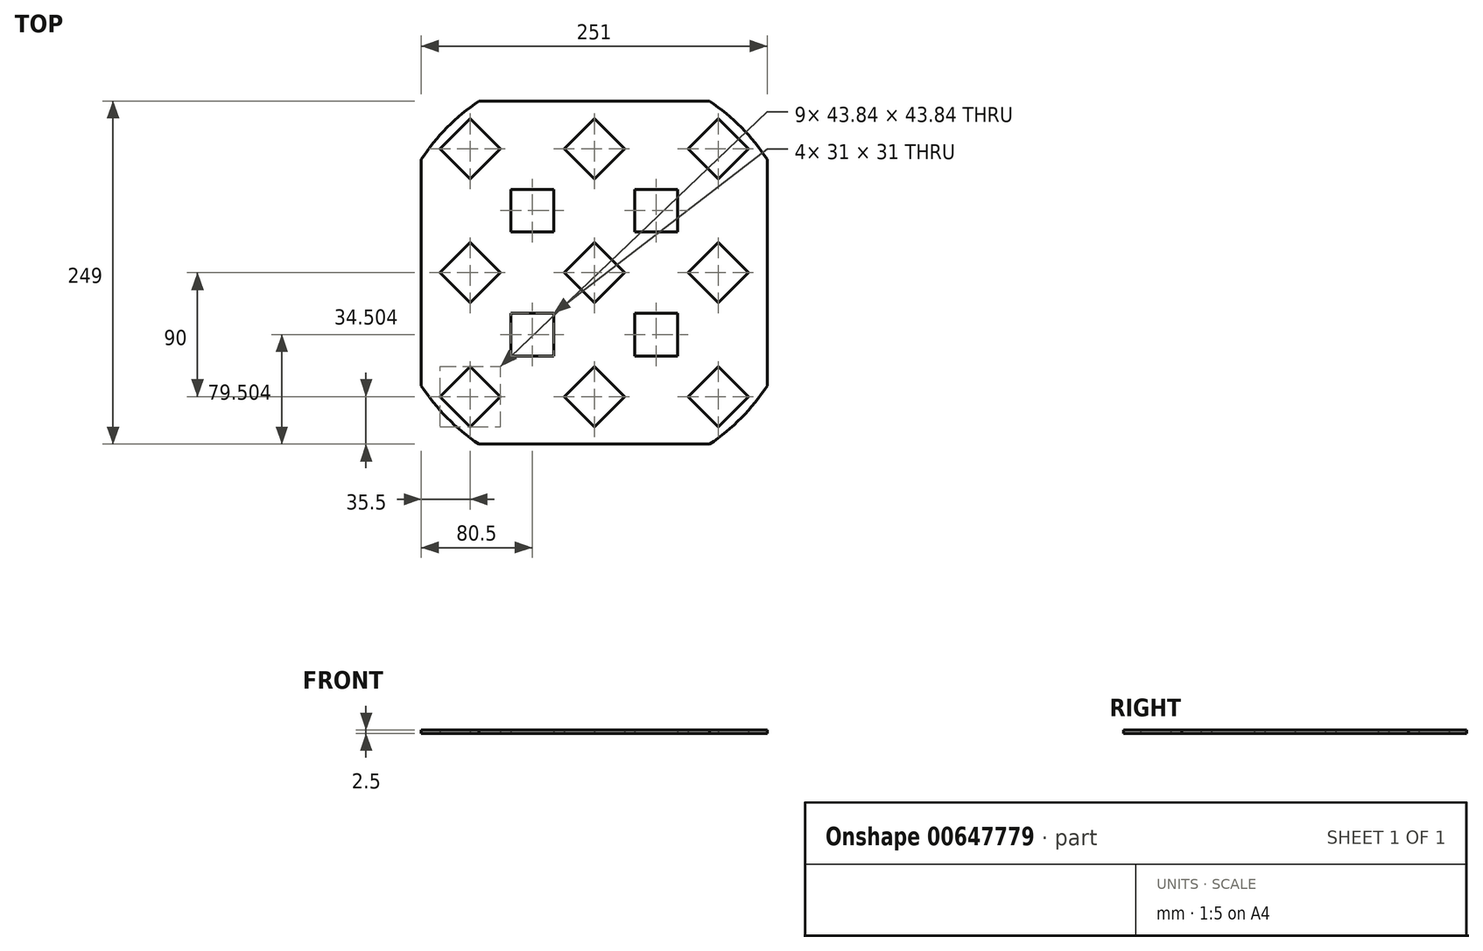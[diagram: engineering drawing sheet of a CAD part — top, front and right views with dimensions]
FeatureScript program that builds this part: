
annotation { "Feature Type Name" : "Feature", "Feature Type Description" : "" }
export const myFeature = defineFeature(function(context is Context, id is Id, definition is map)
    precondition{}
    {
        {
            var Q0;
            Q0=qCreatedBy(makeId("Top.planeOp"),FACE);
            var sketch = newSketch(context, id + "F0", { "sketchPlane" : qUnion([Q0])});
            skLineSegment(sketch, "E0.bottom", {"start": v(6.34, 193.08) * mm, "end": v(173.66, 193.08) * mm});
            skLineSegment(sketch, "E0.right", {"start": v(215.5, 150.74) * mm, "end": v(215.5, -13.57) * mm});
            skLineSegment(sketch, "E1", {"start": v(180, 210.84) * mm, "end": v(180, -126.28) * mm, "construction": true});
            skLineSegment(sketch, "E2", {"start": v(0, 225.22) * mm, "end": v(0, -114.29) * mm, "construction": true});
            skLineSegment(sketch, "E3", {"start": v(-104.9, 158.58) * mm, "end": v(302.2, 158.58) * mm, "construction": true});
            skLineSegment(sketch, "E4", {"start": v(-114.28, -21.42) * mm, "end": v(305.7, -21.42) * mm, "construction": true});
            skLineSegment(sketch, "E5", {"start": v(90, 224) * mm, "end": v(90, -138.86) * mm, "construction": true});
            skLineSegment(sketch, "E6", {"start": v(-107.4, 68.58) * mm, "end": v(321.85, 68.58) * mm, "construction": true});
            skCircle(sketch, "E7.cCircle", {"center": v(0, 158.58) * mm, "radius": 15.5 * mm, "construction": true});
            skLineSegment(sketch, "E7.0", {"start": v(-21.92, 158.58) * mm, "end": v(0, 180.5) * mm});
            skLineSegment(sketch, "E7.1", {"start": v(0, 180.5) * mm, "end": v(21.92, 158.58) * mm});
            skLineSegment(sketch, "E7.2", {"start": v(21.92, 158.58) * mm, "end": v(0, 136.66) * mm});
            skLineSegment(sketch, "E7.3", {"start": v(0, 136.66) * mm, "end": v(-21.92, 158.58) * mm});
            skPoint(sketch, "E7.0.midPoint", {"position": v(-10.96, 169.54) * mm});
            skCircle(sketch, "E8.cCircle", {"center": v(90, 158.58) * mm, "radius": 15.5 * mm, "construction": true});
            skLineSegment(sketch, "E8.0", {"start": v(68.08, 158.58) * mm, "end": v(90, 180.5) * mm});
            skLineSegment(sketch, "E8.1", {"start": v(90, 180.5) * mm, "end": v(111.92, 158.58) * mm});
            skLineSegment(sketch, "E8.2", {"start": v(111.92, 158.58) * mm, "end": v(90, 136.66) * mm});
            skLineSegment(sketch, "E8.3", {"start": v(90, 136.66) * mm, "end": v(68.08, 158.58) * mm});
            skPoint(sketch, "E8.0.midPoint", {"position": v(79.04, 169.54) * mm});
            skCircle(sketch, "E9.cCircle", {"center": v(180, 158.58) * mm, "radius": 15.5 * mm, "construction": true});
            skLineSegment(sketch, "E9.0", {"start": v(158.08, 158.58) * mm, "end": v(180, 180.5) * mm});
            skLineSegment(sketch, "E9.1", {"start": v(180, 180.5) * mm, "end": v(201.92, 158.58) * mm});
            skLineSegment(sketch, "E9.2", {"start": v(201.92, 158.58) * mm, "end": v(180, 136.66) * mm});
            skLineSegment(sketch, "E9.3", {"start": v(180, 136.66) * mm, "end": v(158.08, 158.58) * mm});
            skPoint(sketch, "E9.0.midPoint", {"position": v(169.04, 169.54) * mm});
            skCircle(sketch, "E10.cCircle", {"center": v(180, 68.58) * mm, "radius": 15.5 * mm, "construction": true});
            skLineSegment(sketch, "E10.0", {"start": v(158.08, 68.58) * mm, "end": v(180, 90.5) * mm});
            skLineSegment(sketch, "E10.1", {"start": v(180, 90.5) * mm, "end": v(201.92, 68.58) * mm});
            skLineSegment(sketch, "E10.2", {"start": v(201.92, 68.58) * mm, "end": v(180, 46.66) * mm});
            skLineSegment(sketch, "E10.3", {"start": v(180, 46.66) * mm, "end": v(158.08, 68.58) * mm});
            skPoint(sketch, "E10.0.midPoint", {"position": v(169.04, 79.54) * mm});
            skCircle(sketch, "E11.cCircle", {"center": v(90, 68.58) * mm, "radius": 15.5 * mm, "construction": true});
            skLineSegment(sketch, "E11.0", {"start": v(68.08, 68.58) * mm, "end": v(90, 90.5) * mm});
            skLineSegment(sketch, "E11.1", {"start": v(90, 90.5) * mm, "end": v(111.92, 68.58) * mm});
            skLineSegment(sketch, "E11.2", {"start": v(111.92, 68.58) * mm, "end": v(90, 46.66) * mm});
            skLineSegment(sketch, "E11.3", {"start": v(90, 46.66) * mm, "end": v(68.08, 68.58) * mm});
            skPoint(sketch, "E11.0.midPoint", {"position": v(79.04, 79.54) * mm});
            skCircle(sketch, "E12.cCircle", {"center": v(0, 68.58) * mm, "radius": 15.5 * mm, "construction": true});
            skLineSegment(sketch, "E12.0", {"start": v(-21.92, 68.58) * mm, "end": v(0, 90.5) * mm});
            skLineSegment(sketch, "E12.1", {"start": v(0, 90.5) * mm, "end": v(21.92, 68.58) * mm});
            skLineSegment(sketch, "E12.2", {"start": v(21.92, 68.58) * mm, "end": v(0, 46.66) * mm});
            skLineSegment(sketch, "E12.3", {"start": v(0, 46.66) * mm, "end": v(-21.92, 68.58) * mm});
            skPoint(sketch, "E12.0.midPoint", {"position": v(-10.96, 79.54) * mm});
            skCircle(sketch, "E13.cCircle", {"center": v(0, -21.42) * mm, "radius": 15.5 * mm, "construction": true});
            skLineSegment(sketch, "E13.0", {"start": v(-21.92, -21.42) * mm, "end": v(0, 0.5) * mm});
            skLineSegment(sketch, "E13.1", {"start": v(0, 0.5) * mm, "end": v(21.92, -21.42) * mm});
            skLineSegment(sketch, "E13.2", {"start": v(21.92, -21.42) * mm, "end": v(0, -43.34) * mm});
            skLineSegment(sketch, "E13.3", {"start": v(0, -43.34) * mm, "end": v(-21.92, -21.42) * mm});
            skPoint(sketch, "E13.0.midPoint", {"position": v(-10.96, -10.46) * mm});
            skCircle(sketch, "E14.cCircle", {"center": v(90, -21.42) * mm, "radius": 15.5 * mm, "construction": true});
            skLineSegment(sketch, "E14.0", {"start": v(90, 0.5) * mm, "end": v(111.92, -21.42) * mm});
            skLineSegment(sketch, "E14.1", {"start": v(111.92, -21.42) * mm, "end": v(90, -43.34) * mm});
            skLineSegment(sketch, "E14.2", {"start": v(90, -43.34) * mm, "end": v(68.08, -21.42) * mm});
            skLineSegment(sketch, "E14.3", {"start": v(68.08, -21.42) * mm, "end": v(90, 0.5) * mm});
            skPoint(sketch, "E14.0.midPoint", {"position": v(100.96, -10.46) * mm});
            skCircle(sketch, "E15.cCircle", {"center": v(180, -21.42) * mm, "radius": 15.5 * mm, "construction": true});
            skLineSegment(sketch, "E15.0", {"start": v(158.08, -21.42) * mm, "end": v(180, 0.5) * mm});
            skLineSegment(sketch, "E15.1", {"start": v(180, 0.5) * mm, "end": v(201.92, -21.42) * mm});
            skLineSegment(sketch, "E15.2", {"start": v(201.92, -21.42) * mm, "end": v(180, -43.34) * mm});
            skLineSegment(sketch, "E15.3", {"start": v(180, -43.34) * mm, "end": v(158.08, -21.42) * mm});
            skPoint(sketch, "E15.0.midPoint", {"position": v(169.04, -10.46) * mm});
            skLineSegment(sketch, "E16", {"start": v(-85.12, 113.58) * mm, "end": v(262.73, 113.58) * mm, "construction": true});
            skLineSegment(sketch, "E17", {"start": v(-121.38, 23.58) * mm, "end": v(303.86, 23.58) * mm, "construction": true});
            skLineSegment(sketch, "E18", {"start": v(45, 228.8) * mm, "end": v(45, -105.67) * mm, "construction": true});
            skLineSegment(sketch, "E19", {"start": v(135, 222.04) * mm, "end": v(135, -108.52) * mm, "construction": true});
            skCircle(sketch, "E20.cCircle", {"center": v(135, 23.58) * mm, "radius": 15.5 * mm, "construction": true});
            skLineSegment(sketch, "E20.0", {"start": v(119.5, 39.08) * mm, "end": v(150.5, 39.08) * mm});
            skLineSegment(sketch, "E20.1", {"start": v(150.5, 39.08) * mm, "end": v(150.5, 8.08) * mm});
            skLineSegment(sketch, "E20.2", {"start": v(150.5, 8.08) * mm, "end": v(119.5, 8.08) * mm});
            skLineSegment(sketch, "E20.3", {"start": v(119.5, 8.08) * mm, "end": v(119.5, 39.08) * mm});
            skPoint(sketch, "E20.0.midPoint", {"position": v(135, 39.08) * mm});
            skCircle(sketch, "E21.cCircle", {"center": v(45, 23.58) * mm, "radius": 15.5 * mm, "construction": true});
            skLineSegment(sketch, "E21.0", {"start": v(29.5, 39.08) * mm, "end": v(60.5, 39.08) * mm});
            skLineSegment(sketch, "E21.1", {"start": v(60.5, 39.08) * mm, "end": v(60.5, 8.08) * mm});
            skLineSegment(sketch, "E21.2", {"start": v(60.5, 8.08) * mm, "end": v(29.5, 8.08) * mm});
            skLineSegment(sketch, "E21.3", {"start": v(29.5, 8.08) * mm, "end": v(29.5, 39.08) * mm});
            skPoint(sketch, "E21.0.midPoint", {"position": v(45, 39.08) * mm});
            skCircle(sketch, "E22.cCircle", {"center": v(45, 113.58) * mm, "radius": 15.5 * mm, "construction": true});
            skLineSegment(sketch, "E22.0", {"start": v(29.5, 129.08) * mm, "end": v(60.5, 129.08) * mm});
            skLineSegment(sketch, "E22.1", {"start": v(60.5, 129.08) * mm, "end": v(60.5, 98.08) * mm});
            skLineSegment(sketch, "E22.2", {"start": v(60.5, 98.08) * mm, "end": v(29.5, 98.08) * mm});
            skLineSegment(sketch, "E22.3", {"start": v(29.5, 98.08) * mm, "end": v(29.5, 129.08) * mm});
            skPoint(sketch, "E22.0.midPoint", {"position": v(45, 129.08) * mm});
            skCircle(sketch, "E23.cCircle", {"center": v(135, 113.58) * mm, "radius": 15.5 * mm, "construction": true});
            skLineSegment(sketch, "E23.0", {"start": v(119.5, 129.08) * mm, "end": v(150.5, 129.08) * mm});
            skLineSegment(sketch, "E23.1", {"start": v(150.5, 129.08) * mm, "end": v(150.5, 98.08) * mm});
            skLineSegment(sketch, "E23.2", {"start": v(150.5, 98.08) * mm, "end": v(119.5, 98.08) * mm});
            skLineSegment(sketch, "E23.3", {"start": v(119.5, 98.08) * mm, "end": v(119.5, 129.08) * mm});
            skPoint(sketch, "E23.0.midPoint", {"position": v(135, 129.08) * mm});
            skArc(sketch, "E24", {"start": v(-35.5, -13.57) * mm, "mid": v(-16.7, -36.84) * mm, "end": v(6.34, -55.92) * mm});
            skLineSegment(sketch, "E25.trimOffspring", {"start": v(-35.5, 150.74) * mm, "end": v(-35.5, -13.57) * mm});
            skPoint(sketch, "E26.orphan", {"position": v(-35.5, 193.08) * mm});
            skPoint(sketch, "E27.orphan", {"position": v(215.5, 193.08) * mm});
            skPoint(sketch, "E28.orphan", {"position": v(215.5, -55.92) * mm});
            skLineSegment(sketch, "E29.trimOffspring", {"start": v(6.34, -55.92) * mm, "end": v(173.66, -55.92) * mm});
            skArc(sketch, "E30.trimOffspring", {"start": v(90, -81.42) * mm, "mid": v(112.76, -79.68) * mm, "end": v(135, -74.5) * mm, "construction": true});
            skArc(sketch, "E31.trimOffspring", {"start": v(173.66, -55.92) * mm, "mid": v(196.7, -36.84) * mm, "end": v(215.5, -13.57) * mm});
            skArc(sketch, "E32.trimOffspring", {"start": v(233.1, 23.58) * mm, "mid": v(240, 68.58) * mm, "end": v(233.1, 113.58) * mm, "construction": true});
            skArc(sketch, "E33.trimOffspring", {"start": v(215.5, 150.74) * mm, "mid": v(196.7, 174) * mm, "end": v(173.66, 193.08) * mm});
            skArc(sketch, "E34.trimOffspring", {"start": v(6.34, 193.08) * mm, "mid": v(-16.7, 174) * mm, "end": v(-35.5, 150.74) * mm});
            skSolve(sketch);
        }
        {
            var Q0;
            Q0 = qSketchRegion(id + "F0", true);
            extrude(context, id + "F1", {"entities" : qUnion([Q0]), "depth" : 2.5 * mm, "offsetDistance" : 25 * mm});
        }
    });
